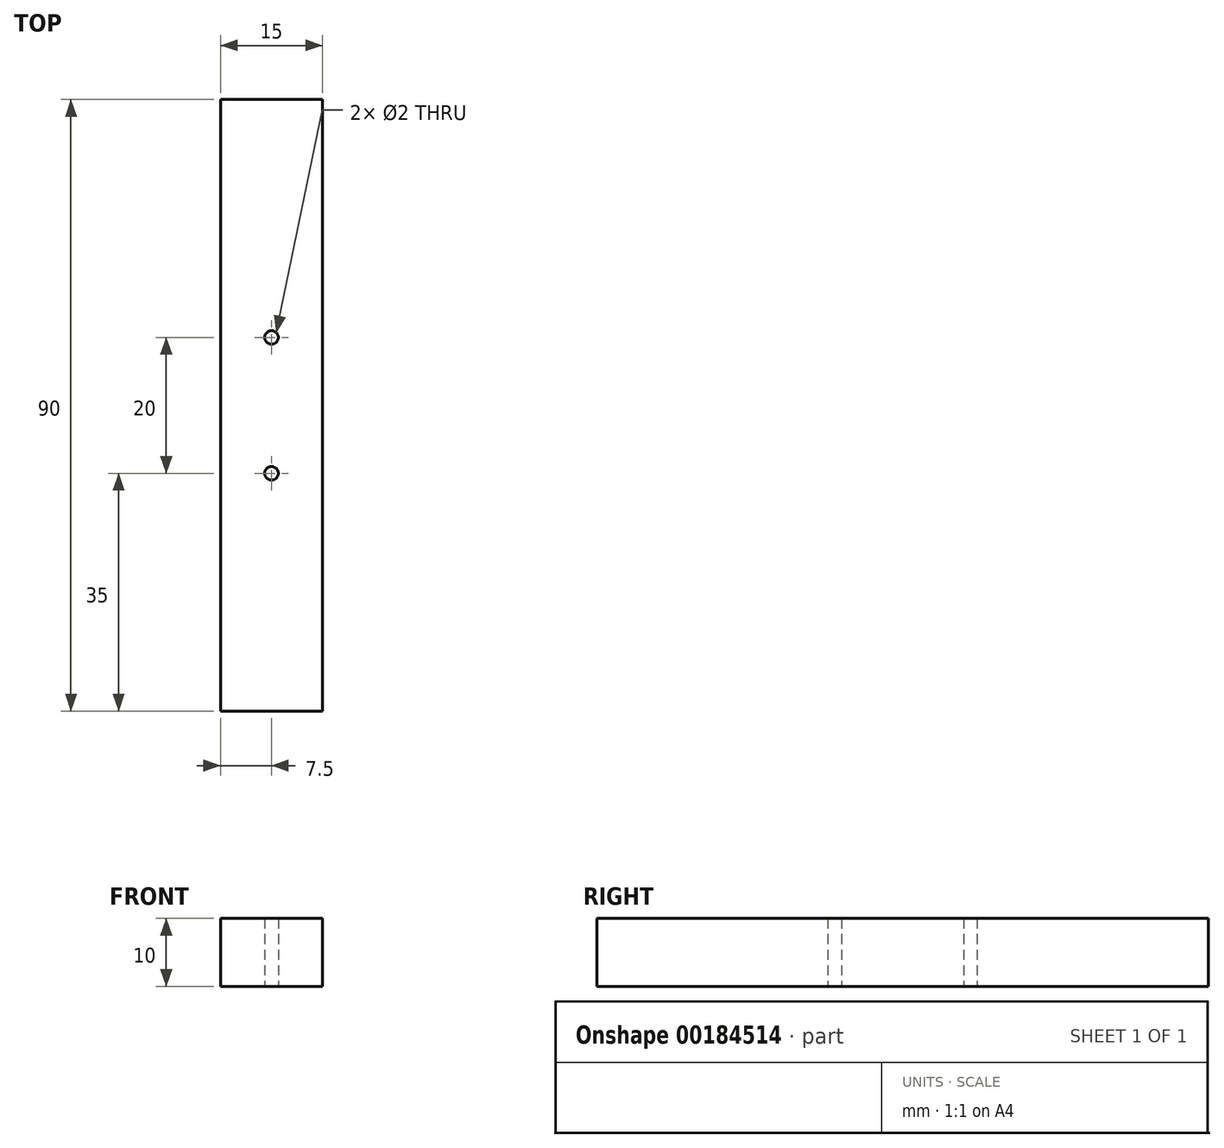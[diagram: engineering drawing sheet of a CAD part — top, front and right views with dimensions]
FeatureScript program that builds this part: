
annotation { "Feature Type Name" : "Feature", "Feature Type Description" : "" }
export const myFeature = defineFeature(function(context is Context, id is Id, definition is map)
    precondition{}
    {
        {
            var Q0;
            Q0=qCreatedBy(makeId("Top.planeOp"),FACE);
            var sketch = newSketch(context, id + "F0", { "sketchPlane" : qUnion([Q0])});
            skLineSegment(sketch, "E0.bottom", {"start": v(0, 0) * mm, "end": v(15, 0) * mm});
            skLineSegment(sketch, "E0.top", {"start": v(0, -90) * mm, "end": v(15, -90) * mm});
            skLineSegment(sketch, "E0.left", {"start": v(0, 0) * mm, "end": v(0, -90) * mm});
            skLineSegment(sketch, "E0.right", {"start": v(15, 0) * mm, "end": v(15, -90) * mm});
            skCircle(sketch, "E1", {"center": v(7.5, -35) * mm, "radius": 1 * mm});
            skCircle(sketch, "E2", {"center": v(7.5, -55) * mm, "radius": 1 * mm});
            skSolve(sketch);
        }
        {
            var Q0;
            Q0 = qSketchRegion(id + "F0", true);
            extrude(context, id + "F1", {"entities" : qUnion([Q0]), "depth" : 10 * mm});
        }
    });
